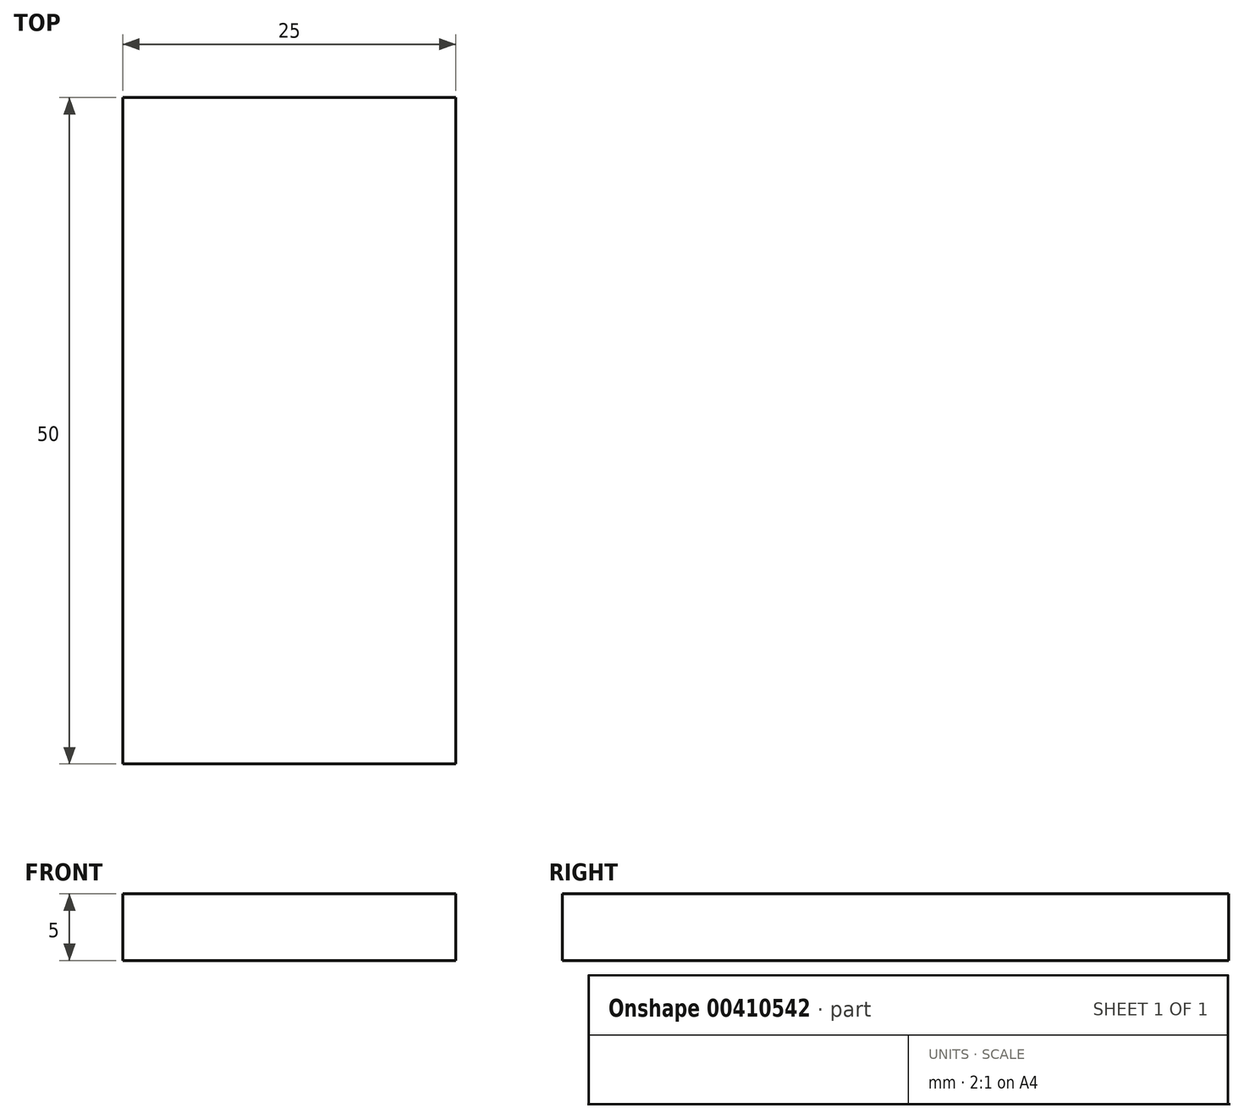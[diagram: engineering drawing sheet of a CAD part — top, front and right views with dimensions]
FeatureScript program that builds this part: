
annotation { "Feature Type Name" : "Feature", "Feature Type Description" : "" }
export const myFeature = defineFeature(function(context is Context, id is Id, definition is map)
    precondition{}
    {
        {
            var Q0;
            Q0=qCreatedBy(makeId("Top.planeOp"),FACE);
            var sketch = newSketch(context, id + "F0", { "sketchPlane" : qUnion([Q0])});
            skLineSegment(sketch, "E0.bottom", {"start": v(12.5, -25) * mm, "end": v(-12.5, -25) * mm});
            skLineSegment(sketch, "E0.top", {"start": v(12.5, 25) * mm, "end": v(-12.5, 25) * mm});
            skLineSegment(sketch, "E0.left", {"start": v(12.5, -25) * mm, "end": v(12.5, 25) * mm});
            skLineSegment(sketch, "E0.right", {"start": v(-12.5, -25) * mm, "end": v(-12.5, 25) * mm});
            skPoint(sketch, "E0.middle", {"position": v(0, 0) * mm});
            skSolve(sketch);
        }
        {
            var Q0;
            Q0=makeQuery(id+"F0.imprint","IMPRINT",FACE,{"disambiguationData":[TD([[makeQuery(id+"F0.imprint","IMPRINT",EDGE,{"derivedFrom":sQuery(id+"F0.wireOp",EDGE,"E0.bottom")}),-1.0]])]});
            extrude(context, id + "F1", {"entities" : qUnion([Q0]), "depth" : 5 * mm});
        }
    });
